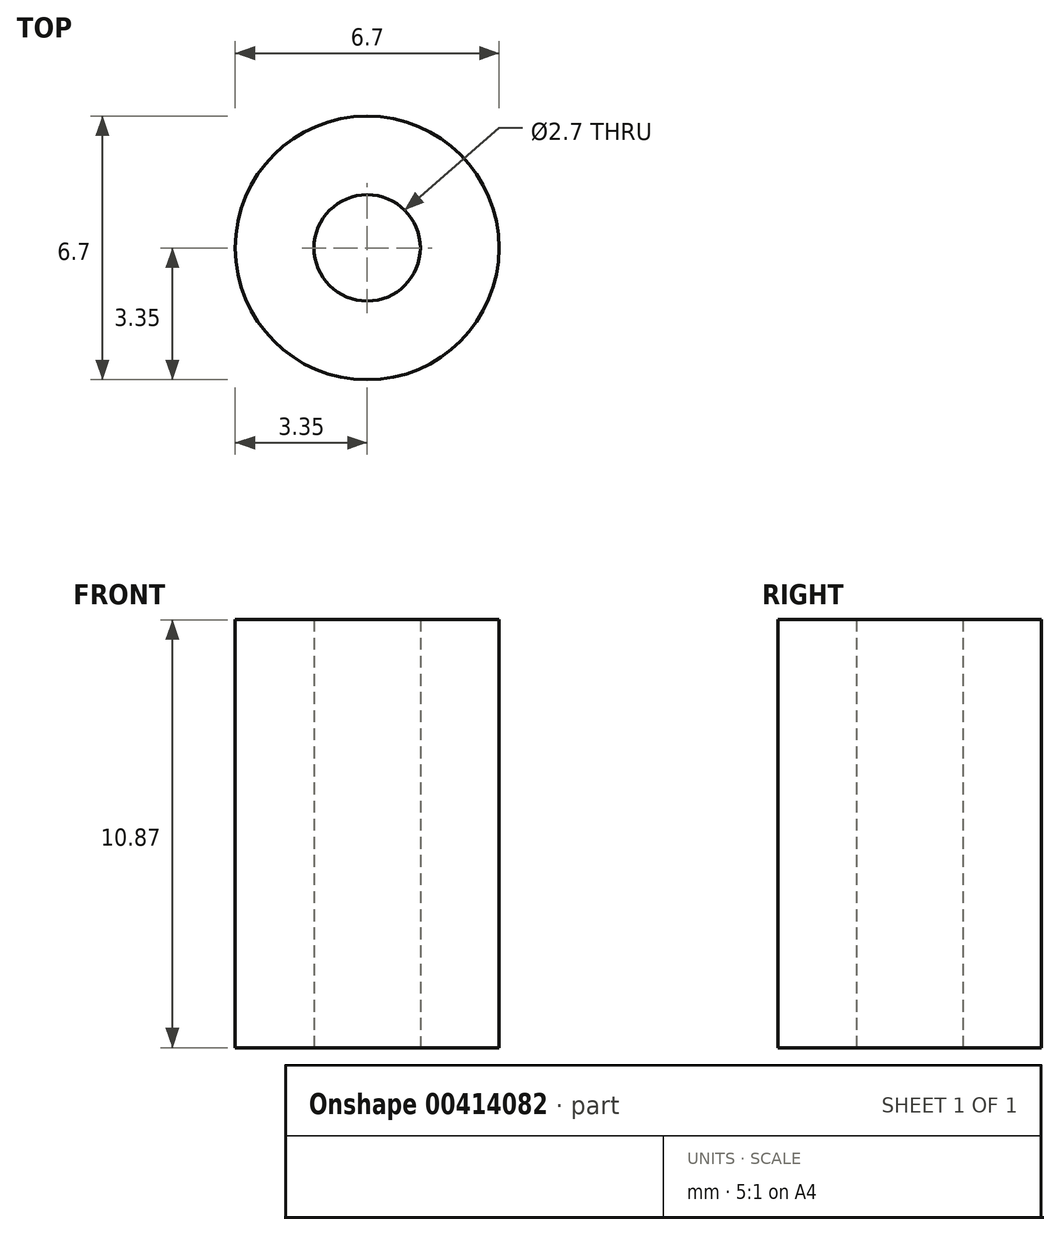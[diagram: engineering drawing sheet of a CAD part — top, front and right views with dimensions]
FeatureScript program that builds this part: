
annotation { "Feature Type Name" : "Feature", "Feature Type Description" : "" }
export const myFeature = defineFeature(function(context is Context, id is Id, definition is map)
    precondition{}
    {
        {
            var Q0;
            Q0=qCreatedBy(makeId("Top.planeOp"),FACE);
            var sketch = newSketch(context, id + "F0", { "sketchPlane" : qUnion([Q0])});
            skCircle(sketch, "E0", {"center": v(0, 0) * mm, "radius": 1.35 * mm});
            skCircle(sketch, "E1", {"center": v(0, 0) * mm, "radius": 3.35 * mm});
            skSolve(sketch);
        }
        {
            var Q0;
            Q0=makeQuery(id+"F0.imprint","IMPRINT",FACE,{"disambiguationData":[TD([[makeQuery(id+"F0.imprint","IMPRINT",EDGE,{"derivedFrom":sQuery(id+"F0.wireOp",EDGE,"E0")}),-1.0]])]});
            extrude(context, id + "F1", {"entities" : qUnion([Q0]), "depth" : 10.87 * mm});
        }
    });
